# Revit family: AVS 250
name_source: partatom
category: Mechanical Equipment
units: mm (PartAtom-declared; Revit-internal decimal feet)

## family parameters
Always vertical = No
Classification = None
Cut with Voids When Loaded = No
Maintain Annotation Orientation = No
OmniClass Number = 23.75.35.17.11
OmniClass Title = Fans for Air Ductwork
Part Type = Breaks Into
Room Calculation Point = No
Round Connector Dimension = Use Diameter
Shared = No
Work Plane-Based = No

## types (1)
- Aventa Silent AVS250
    Apparent Power = 177 VA
    Current = 1 A
    D = 250 mm  [stored 0.82021 ft]
    D1 = 358 mm  [stored 1.17454 ft]
    Dd12 = 1 mm  [stored 0.00328084 ft]
    Dd13 = 2 mm  [stored 0.00656168 ft]
    Dd14 = 6 mm  [stored 0.019685 ft]
    Dd16 = 52 mm
    Dd22 = 5 mm  [stored 0.0164042 ft]
    Dd23 = 6 mm  [stored 0.019685 ft]
    Dd24 = 30 mm  [stored 0.0984252 ft]
    Dd26 = 52 mm
    Default Elevation = 0 mm  [stored 0 ft]
    Description = Inline mixed-flow fan suitable for domestic and light commercial facilities
    Distribution Box Material = Distribution Box Dark Grey
    Duct Connection Size = 250 mm  [stored 0.82021 ft]
    ElBoxH = 53 mm  [stored 0.173885 ft]
    ElBoxL = 104 mm
    ElBoxR = 15 mm  [stored 0.0492126 ft]
    ElBoxW = 104 mm
    Family Version = 1.0
    Fan Material = Metal Black
    Hanger Material = Metal Zinc
    HangerBaseH = 182 mm  [stored 0.597113 ft]
    HangerExtraL = No
    HangerH = 182 mm  [stored 0.597113 ft]
    HangerL = 402 mm  [stored 1.3189 ft]
    HangerL1 = 332 mm  [stored 1.08924 ft]
    HangerW = 150 mm  [stored 0.492126 ft]
    L = 658 mm  [stored 2.15879 ft]
    L1 = 32 mm  [stored 0.104987 ft]
    L11 = 176 mm  [stored 0.577428 ft]
    L12 = 3 mm  [stored 0.00984252 ft]
    L13 = 4 mm  [stored 0.0131234 ft]
    L14 = 10 mm  [stored 0.0328084 ft]
    L15 = 144 mm  [stored 0.472441 ft]
    L16 = 6 mm  [stored 0.019685 ft]
    L17 = 9 mm  [stored 0.0295276 ft]
    L2 = 32 mm  [stored 0.104987 ft]
    L21 = 218 mm  [stored 0.715223 ft]
    L22 = 8 mm  [stored 0.0262467 ft]
    L23 = 13 mm
    L24 = 23 mm  [stored 0.0754593 ft]
    L25 = 159 mm
    L26 = 6 mm  [stored 0.019685 ft]
    L27 = 9 mm  [stored 0.0295276 ft]
    Load Classification = HVAC
    Maintenance Zone Height = 600 mm  [stored 1.9685 ft]
    Maintenance Zone Length = 600 mm  [stored 1.9685 ft]
    Maintenance Zone Length Calc = 658 mm  [stored 2.15879 ft]
    Maintenance Zone Material = Maintenance Zone
    Maintenance Zone Width = 600 mm  [stored 1.9685 ft]
    Manufacturer = Airflow
    Maximum Air Flow = 1400 m³/h
    Model = Aventa Silent AVS250
    Noise Level at 3 m (dBa) = 38
    Number of Poles = 1
    Power = 177 W
    Power Factor = 1
    Protection rating = IPX4
    R1 = 179 mm  [stored 0.58727 ft]
    RPM (min-1) = 2440
    Transported Air Temperature (°C) = -25...+60
    Type Comments = Inline fan single speed up to 1400m3/h
    URL = https://www.airflow.com
    Voltage = 230 V
    Weight = 15.00 kg

note: [stored X ft] marks values corroborated as IEEE doubles in the binary element streams (Revit-internal decimal feet)

## geometry (parser evidence)
native form markers: Sweep x11
no freeform markers — native parametric forms only
